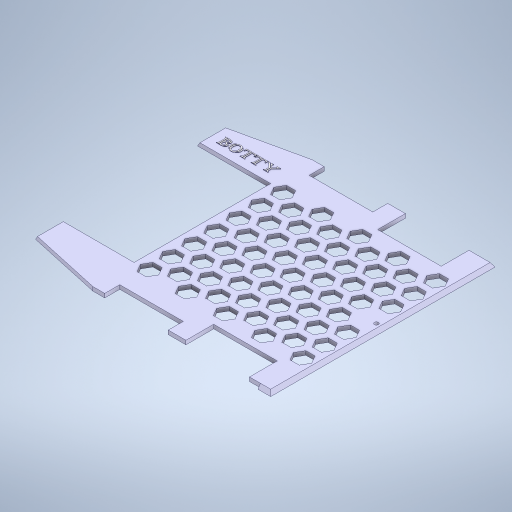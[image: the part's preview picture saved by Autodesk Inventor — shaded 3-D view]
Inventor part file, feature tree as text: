
AUTODESK INVENTOR PART (.ipt)
format: ipt  version: 2024 (Build 280153000, 153)  size: 2,630,656 bytes
history: native  units: in
note: dims shown in document units (in); Inventor stores cm internally (conversion verified against a paired STEP export)
features: sketch x14, extrude x11, projected_geometry x6, plane x3, mirror x2, emboss x2, chamfer x1
ambient origin geometry x8: Origin, YZ Plane, XZ Plane, XY Plane, X Axis, Y Axis, Z Axis, Center Point
bodies: Solid1 (feature_tree)
feature tree (39):
  extrude  "Extrusion1"  Depth=2.2276in
  chamfer  "Chamfer1"  Distance=0.125in
  extrude  "Extrusion2"  Depth=5.6735in
  extrude  "Extrusion3"  Depth=0.8559in
  extrude  "Extrusion4"  Depth=0.8in
  sketch  "Sketch5"  dims[d16=0.0625in d17=0.0in d18=0.8in]
  plane  "Work Plane1"
  plane  "Work Plane2"
  extrude  "Extrusion5"  Depth=0.8in
  extrude  "Extrusion6"  TaperAngle=0.0deg  [1 undecoded]
  plane  "Work Plane3"
  mirror  "Mirror1"
  extrude  "Extrusion7"  TaperAngle=90.0deg  [1 undecoded]
  mirror  "Mirror2"
  sketch  "Sketch9"  dims[d29=90.0deg d30=0.5in]
  extrude  "Extrusion9"  Depth=0.5in
  extrude  "Extrusion10"  TaperAngle=0.0deg  [1 undecoded]
  extrude  "Extrusion11"  Depth=0.8in
  extrude  "Extrusion13"  Depth=0.25in
  emboss  "Emboss2"
  emboss  "Emboss1"
  sketch  "Sketch1"  dims[d0=6.9552in d2=2.2276in]
  sketch  "Sketch2"  dims[d3=4.25in d4=0.125in d5=0.0in]
  projected_geometry  "Projected Loop1"
  sketch  "Sketch3"  dims[d6=0.0851in d7=0.125in d8=0.3832in d9=5.6735in d10=0.8559in]
  projected_geometry  "Projected Loop2"
  sketch  "Sketch4"  dims[d11=5.6735in d12=0.8559in]
  sketch  "Sketch6"  dims[d19=0.5in d20=0.8in]
  sketch  "Sketch7"  dims[d21=0.5in d22=0.0in d23=0.0in]
  sketch  "Sketch8"  dims[d26=11.986in d27=0.0in d28=90.0deg]
  sketch  "Sketch11"  dims[d31=0.8in d32=0.0in d33=0.0in]
  projected_geometry  "Projected Loop4"
  projected_geometry  "Projected Loop5"
  sketch  "Sketch12"  dims[d34=0.5in d35=0.8in]
  sketch  "Sketch13"  dims[d36=0.0in d37=0.0in d38=0.25in]
  sketch  "Sketch16"  dims[d39=0.4in]
  projected_geometry  "Projected Loop7"
  projected_geometry  "Projected Loop8"
  sketch  "Sketch17"  dims[d40=0.25in d41=0.4in d42=0.4in d43=0.0in d44=0.45in d45=0.85in d50=2.1791in d52=7.9317in d53=5.6735in d54=0.025in d55=0.0625in d56=0.25in d57=0.4in d58=0.0in d59=0.0in d60=2.5807in d61=2.0in d62=2.0in d63=2.5557in d67=0.0in d68=0.0in d69=0.38in d70=0.125in d71=0.125in d72=0.0in d73=0.0in d74=0.01in d75=0.0in d150=0.5in d151=0.5in d152=0.5in d153=0.5in d154=0.2in d155=0.2in d156=0.2in d158=0.2in d159=0.2in d160=1.1811in d162=1.4in d163=1.5748in d165=1.2in d168=0.15in d169=0.5in d170=0.5in d171=1.2in d174=0.5in d175=0.5in d187=0.5in d188=0.5in d189=0.5in d191=0.5in d192=0.5in d193=0.5in d195=0.2in d196=0.2in d199=0.2in d202=0.0in d203=0.0in d205=1.85in d206=0.2in d207=0.0157in d208=0.0in]
note: 3 required parameter values undecoded (feature->parameter linkage not recoverable at this tier; creation-order binding heuristic only, values carry confidence <= 0.55)
